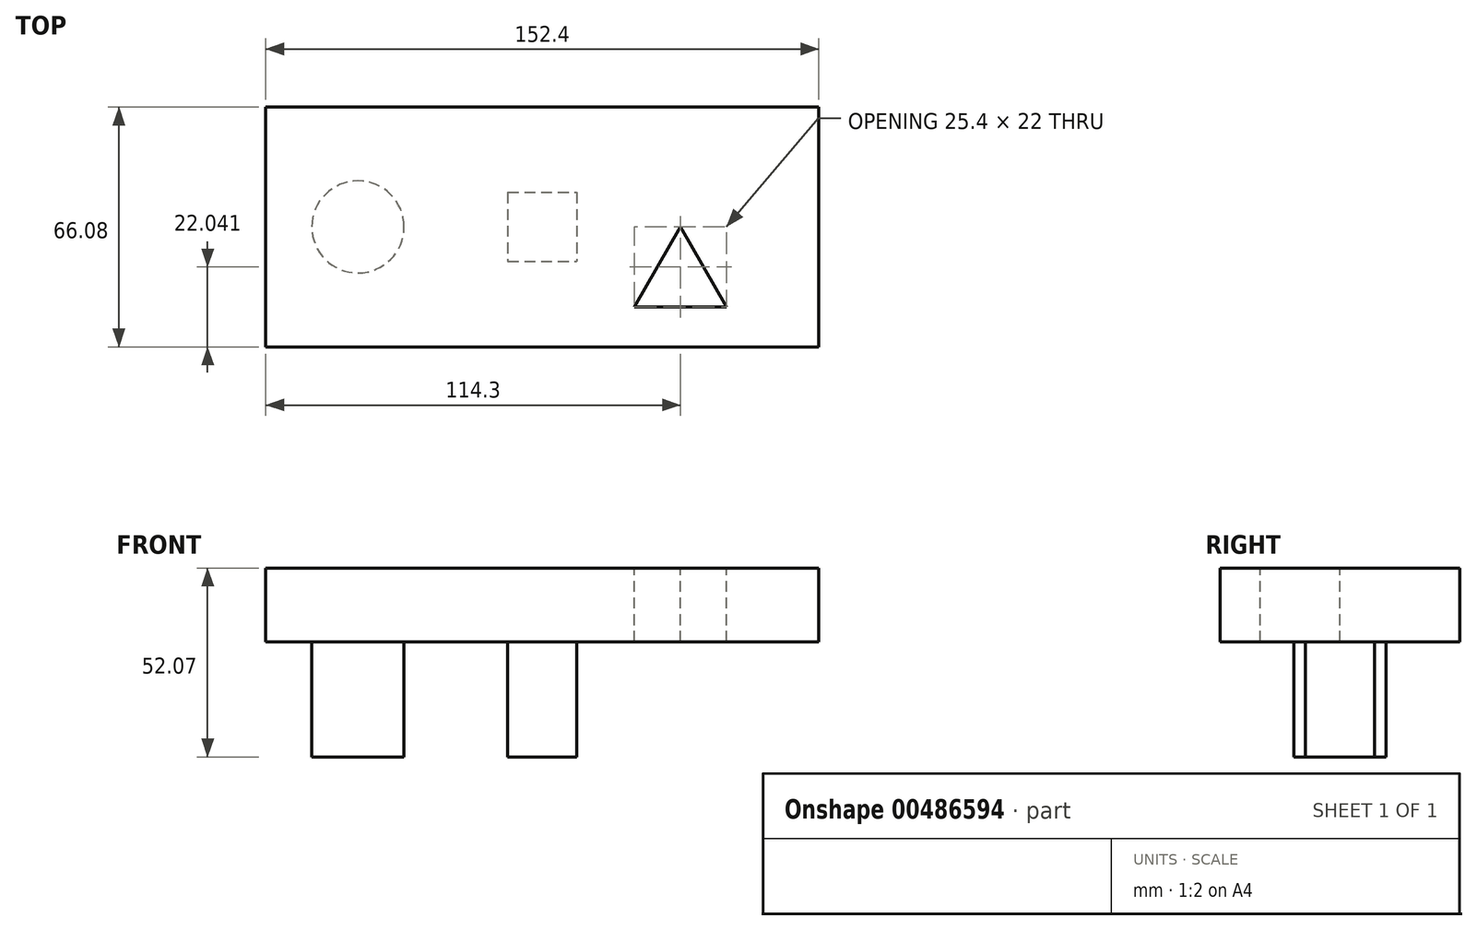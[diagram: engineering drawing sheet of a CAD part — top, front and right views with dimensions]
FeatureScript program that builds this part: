
annotation { "Feature Type Name" : "Feature", "Feature Type Description" : "" }
export const myFeature = defineFeature(function(context is Context, id is Id, definition is map)
    precondition{}
    {
        {
            var Q0;
            Q0=qCreatedBy(makeId("Top.planeOp"),FACE);
            var sketch = newSketch(context, id + "F0", { "sketchPlane" : qUnion([Q0])});
            skLineSegment(sketch, "E0", {"start": v(0, 0) * mm, "end": v(-31.75, 0) * mm});
            skLineSegment(sketch, "E1.bottom", {"start": v(-107.95, 33.04) * mm, "end": v(44.45, 33.04) * mm});
            skLineSegment(sketch, "E1.top", {"start": v(-107.95, -33.04) * mm, "end": v(44.45, -33.04) * mm});
            skLineSegment(sketch, "E1.left", {"start": v(-107.95, 33.04) * mm, "end": v(-107.95, -33.04) * mm});
            skLineSegment(sketch, "E1.right", {"start": v(44.45, 33.04) * mm, "end": v(44.45, -33.04) * mm});
            skPoint(sketch, "E1.middle", {"position": v(-31.75, 0) * mm});
            skLineSegment(sketch, "E2", {"start": v(-31.75, 0) * mm, "end": v(-82.55, 0) * mm});
            skCircle(sketch, "E3", {"center": v(-82.55, 0) * mm, "radius": 12.7 * mm});
            skLineSegment(sketch, "E4.bottom", {"start": v(-41.27, 9.53) * mm, "end": v(-22.22, 9.53) * mm});
            skLineSegment(sketch, "E4.top", {"start": v(-41.27, -9.52) * mm, "end": v(-22.23, -9.52) * mm});
            skLineSegment(sketch, "E4.left", {"start": v(-41.27, 9.53) * mm, "end": v(-41.27, -9.52) * mm});
            skLineSegment(sketch, "E4.right", {"start": v(-22.22, 9.53) * mm, "end": v(-22.23, -9.52) * mm});
            skLineSegment(sketch, "E5", {"start": v(0, 0) * mm, "end": v(6.35, 0) * mm});
            skLineSegment(sketch, "E6", {"start": v(-6.35, -22) * mm, "end": v(19.05, -22) * mm});
            skLineSegment(sketch, "E7", {"start": v(6.35, 0) * mm, "end": v(-6.35, -22) * mm});
            skLineSegment(sketch, "E8", {"start": v(6.35, 0) * mm, "end": v(19.05, -22) * mm});
            skSolve(sketch);
        }
        {
            var Q0;
            Q0=makeQuery(id+"F0.imprint","IMPRINT",FACE,{"disambiguationData":[TD([[makeQuery(id+"F0.imprint","IMPRINT",EDGE,{"derivedFrom":sQuery(id+"F0.wireOp",EDGE,"E1.bottom")}),-1.0]])]});
            extrude(context, id + "F1", {"entities" : qUnion([Q0]), "oppositeDirection" : true, "depth" : 20.32 * mm});
        }
        {
            var Q0;
            {var subQ0=sQuery(id+"F0.wireOp",EDGE,"E4.top");Q0=makeQuery(id+"F0.imprint","IMPRINT",FACE,{"disambiguationData":[TD([[makeQuery(id+"F0.imprint","IMPRINT",EDGE,{"derivedFrom":subQ0}),1.0]])]});}
            var Q1;
            {var subQ1=sQuery(id+"F0.wireOp",EDGE,"E4.bottom");Q1=makeQuery(id+"F0.imprint","IMPRINT",FACE,{"disambiguationData":[TD([[makeQuery(id+"F0.imprint","IMPRINT",EDGE,{"derivedFrom":subQ1}),-1.0]])]});}
            var Q2;
            Q2=makeQuery(id+"F0.imprint","IMPRINT",FACE,{"disambiguationData":[TD([[makeQuery(id+"F0.imprint","IMPRINT",EDGE,{"derivedFrom":sQuery(id+"F0.wireOp",EDGE,"E3")}),1.0]])]});
            extrude(context, id + "F2", {"entities" : qUnion([Q0, Q1, Q2]), "operationType" : NewBodyOperationType.ADD, "oppositeDirection" : true, "depth" : 52.07 * mm});
        }
    });
